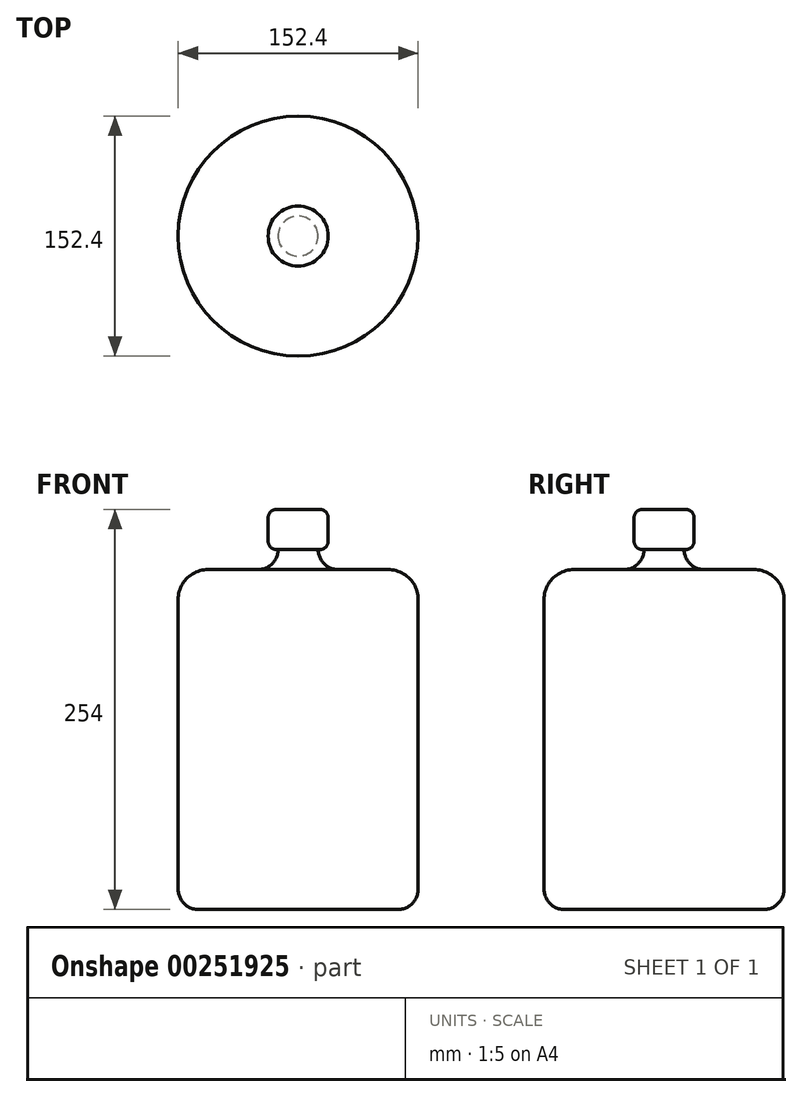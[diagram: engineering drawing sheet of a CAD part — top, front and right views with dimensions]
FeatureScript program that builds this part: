
annotation { "Feature Type Name" : "Feature", "Feature Type Description" : "" }
export const myFeature = defineFeature(function(context is Context, id is Id, definition is map)
    precondition{}
    {
        {
            var Q0;
            Q0=qCreatedBy(makeId("Front.planeOp"),FACE);
            var sketch = newSketch(context, id + "F0", { "sketchPlane" : qUnion([Q0])});
            skLineSegment(sketch, "E0", {"start": v(0, 157.62) * mm, "end": v(0, -186.63) * mm, "construction": true});
            skLineSegment(sketch, "E1", {"start": v(0, -186.63) * mm, "end": v(-76.2, -186.63) * mm});
            skLineSegment(sketch, "E2", {"start": v(-76.2, -186.63) * mm, "end": v(-76.2, -173.93) * mm});
            skLineSegment(sketch, "E3", {"start": v(-76.2, -173.93) * mm, "end": v(0, -173.93) * mm});
            skLineSegment(sketch, "E4", {"start": v(-76.2, -173.93) * mm, "end": v(-76.2, 29.27) * mm});
            skLineSegment(sketch, "E5", {"start": v(-76.2, 29.27) * mm, "end": v(0, 29.27) * mm});
            skLineSegment(sketch, "E6", {"start": v(0, 29.27) * mm, "end": v(0, -186.63) * mm});
            skLineSegment(sketch, "E7", {"start": v(0, 29.27) * mm, "end": v(-12.7, 29.27) * mm});
            skLineSegment(sketch, "E8", {"start": v(-12.7, 29.27) * mm, "end": v(-12.7, 41.97) * mm});
            skLineSegment(sketch, "E9", {"start": v(-12.7, 41.97) * mm, "end": v(0, 41.97) * mm});
            skLineSegment(sketch, "E10", {"start": v(0, 41.97) * mm, "end": v(0, 29.27) * mm});
            skLineSegment(sketch, "E11", {"start": v(-12.7, 41.97) * mm, "end": v(-19.05, 41.97) * mm});
            skLineSegment(sketch, "E12", {"start": v(-19.05, 41.97) * mm, "end": v(-19.05, 67.37) * mm});
            skLineSegment(sketch, "E13", {"start": v(0, 61.02) * mm, "end": v(0, 41.97) * mm});
            skLineSegment(sketch, "E14", {"start": v(-19.05, 67.37) * mm, "end": v(0, 67.37) * mm});
            skLineSegment(sketch, "E15", {"start": v(0, 61.02) * mm, "end": v(0, 67.37) * mm});
            skLineSegment(sketch, "E16", {"start": v(0, 67.37) * mm, "end": v(0, 35.62) * mm});
            skSolve(sketch);
        }
        {
            var Q0;
            Q0 = qSketchRegion(id + "F0", true);
            var Q1;
            Q1=sQuery(id+"F0.wireOp",EDGE,"E0");
            revolve(context, id + "F1", {"entities" : qUnion([Q0]), "axis" : qUnion([Q1]), "revolveType" : RevolveType.FULL});
        }
        {
            var Q0;
            Q0=makeQuery(id+"F1.opRevolve","SWEPT_EDGE",EDGE,{"disambiguationData":[OSD([sQuery(id+"F0.wireOp",EDGE,"E4"),sQuery(id+"F0.wireOp",EDGE,"E5")])]});
            fillet(context, id + "F2", {"entities" : qUnion([Q0]), "radius" : 19.05 * mm, "tangentPropagation" : true, "allowEdgeOverflow" : false});
        }
        {
            var Q0;
            Q0=makeQuery(id+"F1.opRevolve","SWEPT_EDGE",EDGE,{"disambiguationData":[OSD([sQuery(id+"F0.wireOp",EDGE,"E1"),sQuery(id+"F0.wireOp",EDGE,"E2")])]});
            fillet(context, id + "F3", {"entities" : qUnion([Q0]), "radius" : 12.7 * mm, "tangentPropagation" : true, "allowEdgeOverflow" : false});
        }
        {
            var Q0;
            Q0=makeQuery(id+"F1.opRevolve","SWEPT_EDGE",EDGE,{"disambiguationData":[OSD([sQuery(id+"F0.wireOp",EDGE,"E5"),sQuery(id+"F0.wireOp",EDGE,"E7"),sQuery(id+"F0.wireOp",EDGE,"E8")])]});
            fillet(context, id + "F4", {"entities" : qUnion([Q0]), "radius" : 12.7 * mm, "tangentPropagation" : true, "allowEdgeOverflow" : false});
        }
        {
            var Q0;
            Q0=makeQuery(id+"F1.opRevolve","SWEPT_EDGE",EDGE,{"disambiguationData":[OSD([sQuery(id+"F0.wireOp",EDGE,"E11"),sQuery(id+"F0.wireOp",EDGE,"E12")])]});
            fillet(context, id + "F5", {"entities" : qUnion([Q0]), "radius" : 5.08 * mm, "tangentPropagation" : true, "allowEdgeOverflow" : false});
        }
        {
            var Q0;
            Q0=makeQuery(id+"F1.opRevolve","SWEPT_EDGE",EDGE,{"disambiguationData":[OSD([sQuery(id+"F0.wireOp",EDGE,"E12"),sQuery(id+"F0.wireOp",EDGE,"E14")])]});
            fillet(context, id + "F6", {"entities" : qUnion([Q0]), "radius" : 5.08 * mm, "tangentPropagation" : true, "allowEdgeOverflow" : false});
        }
    });
